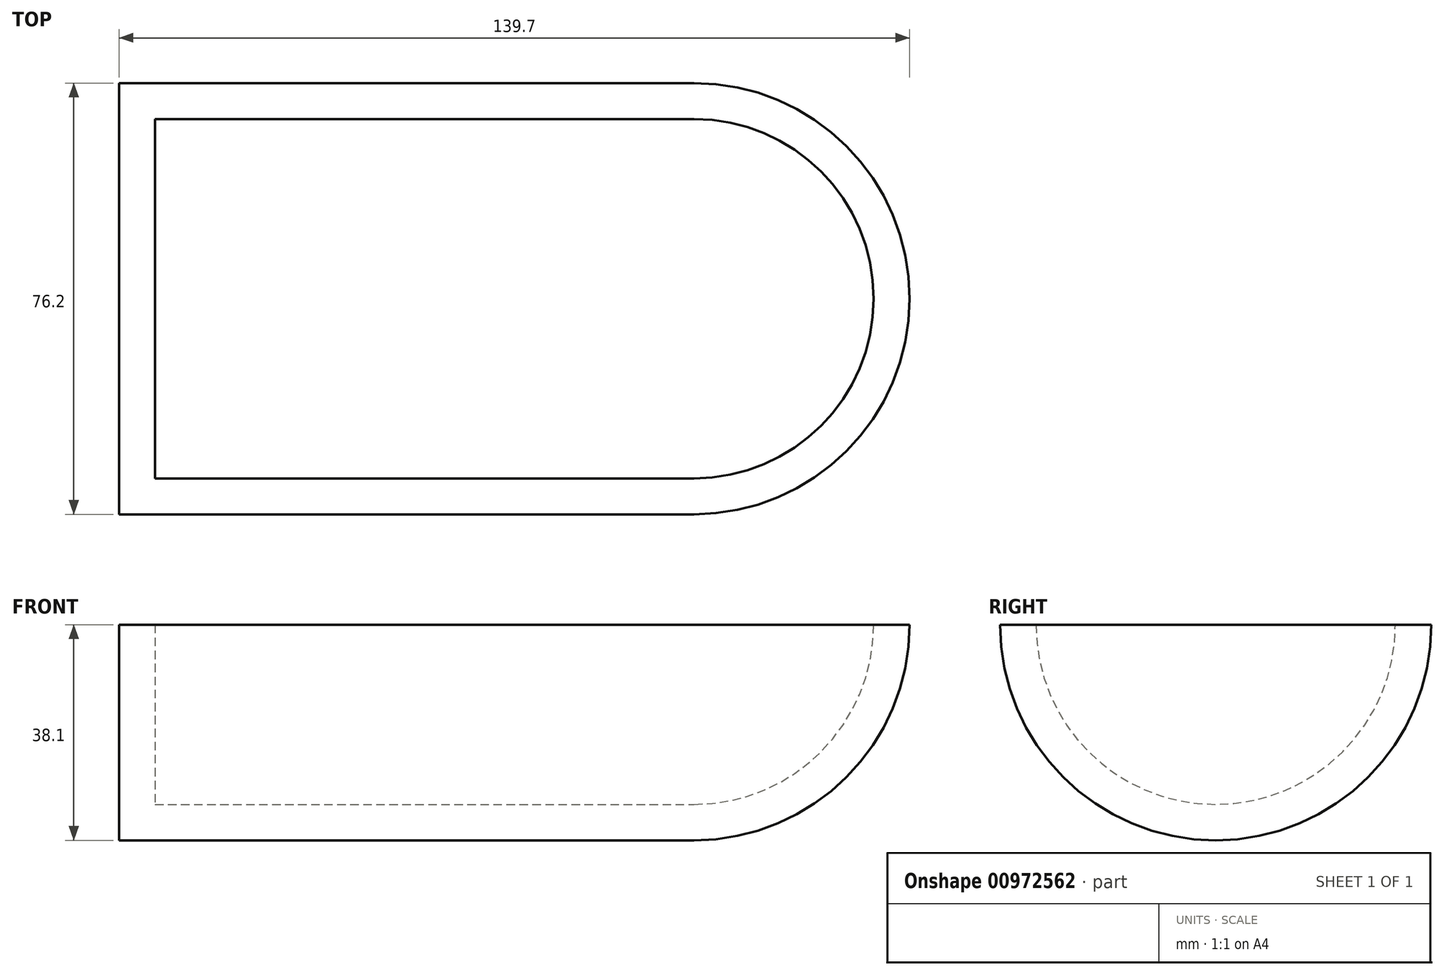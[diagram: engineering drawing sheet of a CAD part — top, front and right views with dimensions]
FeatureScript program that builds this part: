
annotation { "Feature Type Name" : "Feature", "Feature Type Description" : "" }
export const myFeature = defineFeature(function(context is Context, id is Id, definition is map)
    precondition{}
    {
        {
            var Q0;
            Q0=qCreatedBy(makeId("Front.planeOp"),FACE);
            var sketch = newSketch(context, id + "F0", { "sketchPlane" : qUnion([Q0])});
            skLineSegment(sketch, "E0.bottom", {"start": v(0, 0) * mm, "end": v(-101.6, 0) * mm});
            skLineSegment(sketch, "E0.top", {"start": v(0, -38.1) * mm, "end": v(-101.6, -38.1) * mm});
            skLineSegment(sketch, "E0.left", {"start": v(0, 0) * mm, "end": v(0, -38.1) * mm});
            skLineSegment(sketch, "E0.right", {"start": v(-101.6, 0) * mm, "end": v(-101.6, -38.1) * mm});
            skArc(sketch, "E1", {"start": v(0, -38.1) * mm, "mid": v(26.94, -26.94) * mm, "end": v(38.1, 0) * mm});
            skLineSegment(sketch, "E2", {"start": v(0, 0) * mm, "end": v(38.1, 0) * mm});
            skLineSegment(sketch, "E3.0", {"start": v(-95.25, 0) * mm, "end": v(-95.25, -31.75) * mm});
            skLineSegment(sketch, "E3.1", {"start": v(0, -31.75) * mm, "end": v(-95.25, -31.75) * mm});
            skArc(sketch, "E3.2", {"start": v(0, -31.75) * mm, "mid": v(22.45, -22.45) * mm, "end": v(31.75, 0) * mm});
            skSolve(sketch);
        }
        {
            var Q0;
            {var subQ2=sQuery(id+"F0.wireOp",EDGE,"E0.top");Q0=makeQuery(id+"F0.imprint","IMPRINT",FACE,{"disambiguationData":[TD([[makeQuery(id+"F0.imprint","IMPRINT",EDGE,{"derivedFrom":subQ2}),-1.0]])]});}
            var Q1;
            {var subQ0=sQuery(id+"F0.wireOp",EDGE,"E1");Q1=makeQuery(id+"F0.imprint","IMPRINT",FACE,{"disambiguationData":[TD([[makeQuery(id+"F0.imprint","IMPRINT",EDGE,{"derivedFrom":subQ0}),1.0]])]});}
            var Q2;
            Q2=sQuery(id+"F0.wireOp",EDGE,"E0.bottom");
            revolve(context, id + "F1", {"surfaceOperationType" : NewSurfaceOperationType.NEW, "entities" : qUnion([Q0, Q1]), "axis" : qUnion([Q2]), "revolveType" : RevolveType.SYMMETRIC, "angle" : 180 * degree});
        }
    });
